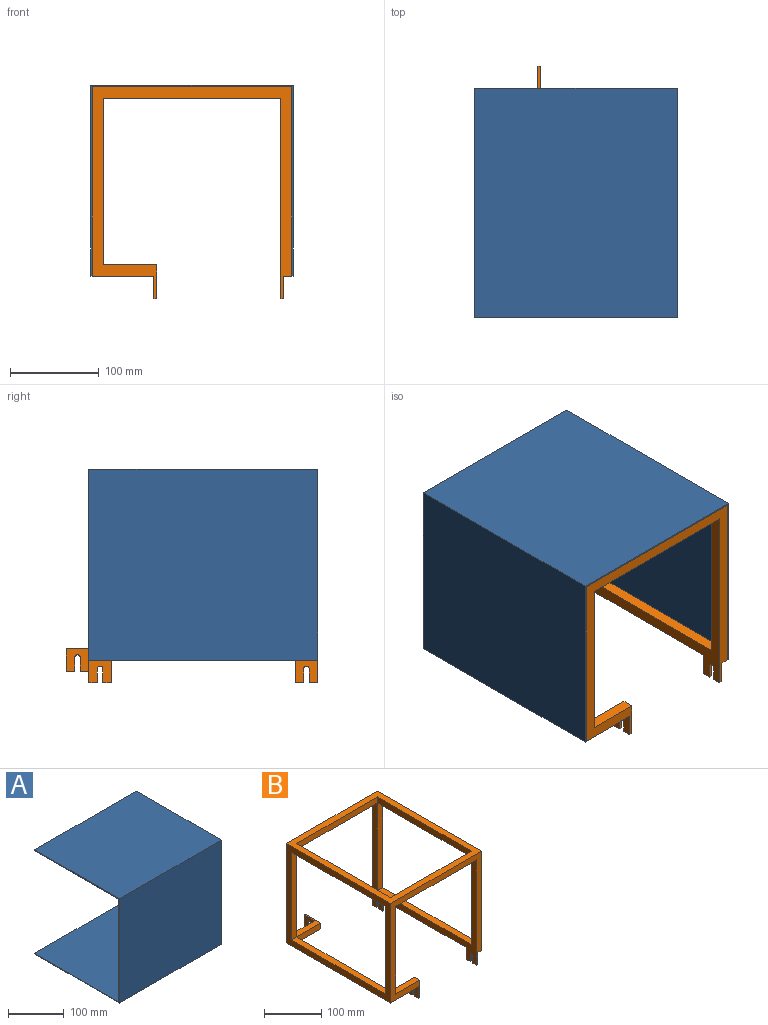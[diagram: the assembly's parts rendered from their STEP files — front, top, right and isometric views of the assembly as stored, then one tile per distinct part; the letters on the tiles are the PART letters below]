
ASSEMBLY  parts=2 mates=1
PART A: 10 faces, bbox 258x215x228.6 mm
  f0: plane 228.58x214.99mm, normal (1,0,0), area 1040.4mm2, adj f1,f3,f4,f5,f6,f7,f8,f9
  f1: plane 258x1.59mm, normal (0,1,0), area 409.6mm2, adj f0,f2,f3,f4
  f2: plane 228.58x214.99mm, normal (-1,0,0), area 1040.4mm2, adj f1,f3,f4,f5,f6,f7,f8,f9
  f3: plane 258x214.99mm, normal (0,0,1), area 55466.8mm2, adj f0,f1,f2,f6
  f4: plane 258x213.4mm, normal (0,0,-1), area 55057.2mm2, adj f0,f1,f2,f5
  f5: plane 258x225.4mm, normal (0,1,0), area 58153.2mm2, adj f0,f2,f4,f7
  f6: plane 258x228.58mm, normal (0,-1,0), area 58972.3mm2, adj f0,f2,f3,f9
  f7: plane 258x213.4mm, normal (0,0,1), area 55057.2mm2, adj f0,f2,f5,f8
  f8: plane 258x1.59mm, normal (0,1,0), area 409.6mm2, adj f0,f2,f7,f9
  f9: plane 258x214.99mm, normal (0,0,-1), area 55466.8mm2, adj f0,f2,f6,f8
PART B: 61 faces, bbox 225.4x283.4x238.8 mm
  f0: plane 9.7x3.18mm, normal (0,0,-1), area 30.8mm2, adj f1,f47,f48,f59
  f1: plane 38.1x25.4mm, normal (1,0,0), area 698.1mm2, adj f0,f9,f11,f28,f45,f46,f47,f58
  f2: plane 9.7x3.18mm, normal (0,0,-1), area 30.8mm2, adj f5,f37,f39,f55
  f3: plane 9.7x3.18mm, normal (0,0,-1), area 30.8mm2, adj f5,f7,f41,f52
  f4: plane 9.7x3.18mm, normal (0,0,-1), area 30.8mm2, adj f6,f8,f23,f49
  f5: plane 258x226.1mm, normal (-1,0,0), area 9125.4mm2, adj f2,f3,f17,f19,f22,f23,f24,f33
  f6: plane 38.1x25.4mm, normal (1,0,0), area 698.1mm2, adj f4,f10,f23,f27,f42,f43,f44,f49
  f7: plane 25.4x25.4mm, normal (1,0,0), area 536.8mm2, adj f3,f17,f24,f40,f41,f52,f53,f54
  f8: plane 25.4x25.4mm, normal (-1,0,0), area 536.8mm2, adj f4,f9,f23,f42,f43,f44,f49,f50
  f9: plane 258x72.7mm, normal (0,0,-1), area 4760.3mm2, adj f1,f8,f13,f16,f23,f24,f27,f28
  f10: plane 60x12.7mm, normal (0,0,1), area 762mm2, adj f6,f15,f23,f27
  f11: plane 60x38.1mm, normal (0,0,1), area 842.6mm2, adj f1,f14,f24,f28,f47,f48
  f12: plane 258x213.4mm, normal (1,0,0), area 11328.4mm2, adj f17,f18,f23,f24,f33,f34,f35,f36
  f13: plane 232.6x12.7mm, normal (1,0,0), area 2954mm2, adj f9,f27,f28,f32
  f14: plane 188x12.7mm, normal (1,0,0), area 2387.6mm2, adj f11,f22,f24,f31
  f15: plane 188x12.7mm, normal (1,0,0), area 2387.6mm2, adj f10,f19,f23,f29
  f16: plane 258x213.4mm, normal (-1,0,0), area 11328.4mm2, adj f9,f18,f23,f24,f29,f30,f31,f32
  f17: plane 258x12.7mm, normal (0,0,-1), area 3115.3mm2, adj f5,f7,f12,f23,f24,f37,f39,f41
  f18: plane 258x225.4mm, normal (0,0,1), area 11633.2mm2, adj f12,f16,f20,f21,f23,f24,f25,f26
  f19: plane 200x12.7mm, normal (0,0,-1), area 2540mm2, adj f5,f15,f23,f26
  f20: plane 232.6x12.7mm, normal (-1,0,0), area 2954mm2, adj f18,f25,f26,f35
  f21: plane 232.6x12.7mm, normal (1,0,0), area 2954mm2, adj f18,f25,f26,f30
  f22: plane 200x12.7mm, normal (0,0,-1), area 2540mm2, adj f5,f14,f24,f25
  f23: plane 238.8x225.4mm, normal (0,-1,0), area 8883.7mm2, adj f4,f5,f6,f8,f9,f10,f12,f15
  f24: plane 238.8x225.4mm, normal (0,1,0), area 8762.7mm2, adj f5,f7,f9,f11,f12,f14,f16,f17
  f25: plane 200x12.7mm, normal (0,-1,0), area 2540mm2, adj f18,f20,f21,f22
  f26: plane 200x12.7mm, normal (0,1,0), area 2540mm2, adj f18,f19,f20,f21
  f27: plane 60x12.7mm, normal (0,1,0), area 762mm2, adj f6,f9,f10,f13,f42
  f28: plane 60x12.7mm, normal (0,-1,0), area 762mm2, adj f1,f9,f11,f13
  f29: plane 188x12.7mm, normal (0,1,0), area 2387.6mm2, adj f15,f16,f30,f32
  f30: plane 232.6x12.7mm, normal (0,0,-1), area 2954mm2, adj f16,f21,f29,f31
  f31: plane 188x12.7mm, normal (0,-1,0), area 2387.6mm2, adj f14,f16,f30,f32
  f32: plane 232.6x12.7mm, normal (0,0,1), area 2954mm2, adj f13,f16,f29,f31
  f33: plane 232.6x12.7mm, normal (0,0,1), area 2954mm2, adj f5,f12,f34,f36
  f34: plane 188x12.7mm, normal (0,-1,0), area 2387.6mm2, adj f5,f12,f33,f35
  f35: plane 232.6x12.7mm, normal (0,0,-1), area 2954mm2, adj f12,f20,f34,f36
  f36: plane 188x12.7mm, normal (0,1,0), area 2387.6mm2, adj f5,f12,f33,f35
  f37: plane 25.4x3.18mm, normal (0,1,0), area 80.6mm2, adj f2,f5,f17,f39
  f38: plane 9.7x3.18mm, normal (0,0,-1), area 30.8mm2, adj f5,f23,f39,f57
  f39: plane 25.4x25.4mm, normal (1,0,0), area 536.8mm2, adj f2,f17,f23,f37,f38,f55,f56,f57
  f40: plane 9.7x3.18mm, normal (0,0,-1), area 30.8mm2, adj f5,f7,f24,f53
  f41: plane 25.4x3.18mm, normal (0,-1,0), area 80.6mm2, adj f3,f5,f7,f17
  f42: plane 12.7x3.18mm, normal (0,0,1), area 40.3mm2, adj f6,f8,f27,f44
  f43: plane 9.7x3.18mm, normal (0,0,-1), area 30.8mm2, adj f6,f8,f44,f51
  f44: plane 25.4x3.18mm, normal (0,1,0), area 80.6mm2, adj f6,f8,f42,f43
  f45: plane 12.7x3.18mm, normal (0,-1,0), area 40.3mm2, adj f1,f9,f46,f48
  f46: plane 9.7x3.18mm, normal (0,0,-1), area 30.8mm2, adj f1,f45,f48,f58
  f47: plane 25.4x3.18mm, normal (0,1,0), area 80.6mm2, adj f0,f1,f11,f48
  f48: plane 25.4x25.4mm, normal (-1,0,0), area 536.8mm2, adj f0,f11,f24,f45,f46,f47,f58,f59
  f49: plane 15.7x3.18mm, normal (0,1,0), area 49.8mm2, adj f4,f6,f8,f50
  f50: cylinder r=3mm len=6mm, axis (1,0,0), area 29.9mm2, adj f6,f8,f49,f51
  f51: plane 15.7x3.18mm, normal (0,-1,0), area 49.8mm2, adj f6,f8,f43,f50
  f52: plane 15.7x3.18mm, normal (0,1,0), area 49.8mm2, adj f3,f5,f7,f54
  f53: plane 15.7x3.18mm, normal (0,-1,0), area 49.8mm2, adj f5,f7,f40,f54
  f54: cylinder r=3mm len=6mm, axis (1,0,0), area 29.9mm2, adj f5,f7,f52,f53
  f55: plane 15.7x3.18mm, normal (0,-1,0), area 49.8mm2, adj f2,f5,f39,f56
  f56: cylinder r=3mm len=6mm, axis (1,0,0), area 29.9mm2, adj f5,f39,f55,f57
  f57: plane 15.7x3.18mm, normal (0,1,0), area 49.8mm2, adj f5,f38,f39,f56
  f58: plane 15.7x3.18mm, normal (0,1,0), area 49.8mm2, adj f1,f46,f48,f60
  f59: plane 15.7x3.18mm, normal (0,-1,0), area 49.8mm2, adj f0,f1,f48,f60
  f60: cylinder r=3mm len=6mm, axis (-1,0,0), area 29.9mm2, adj f1,f48,f58,f59
PLACE A rot(axis=(-0.58,-0.58,0.58),120deg) t=(-106.59,-7.39,15.37)mm
PLACE B t=(6.11,121.61,15.37)mm fixed
MATE fastened A.f4 <-> B.f16  axis (1,0,0) through (-106.59,-7.39,15.37)mm
